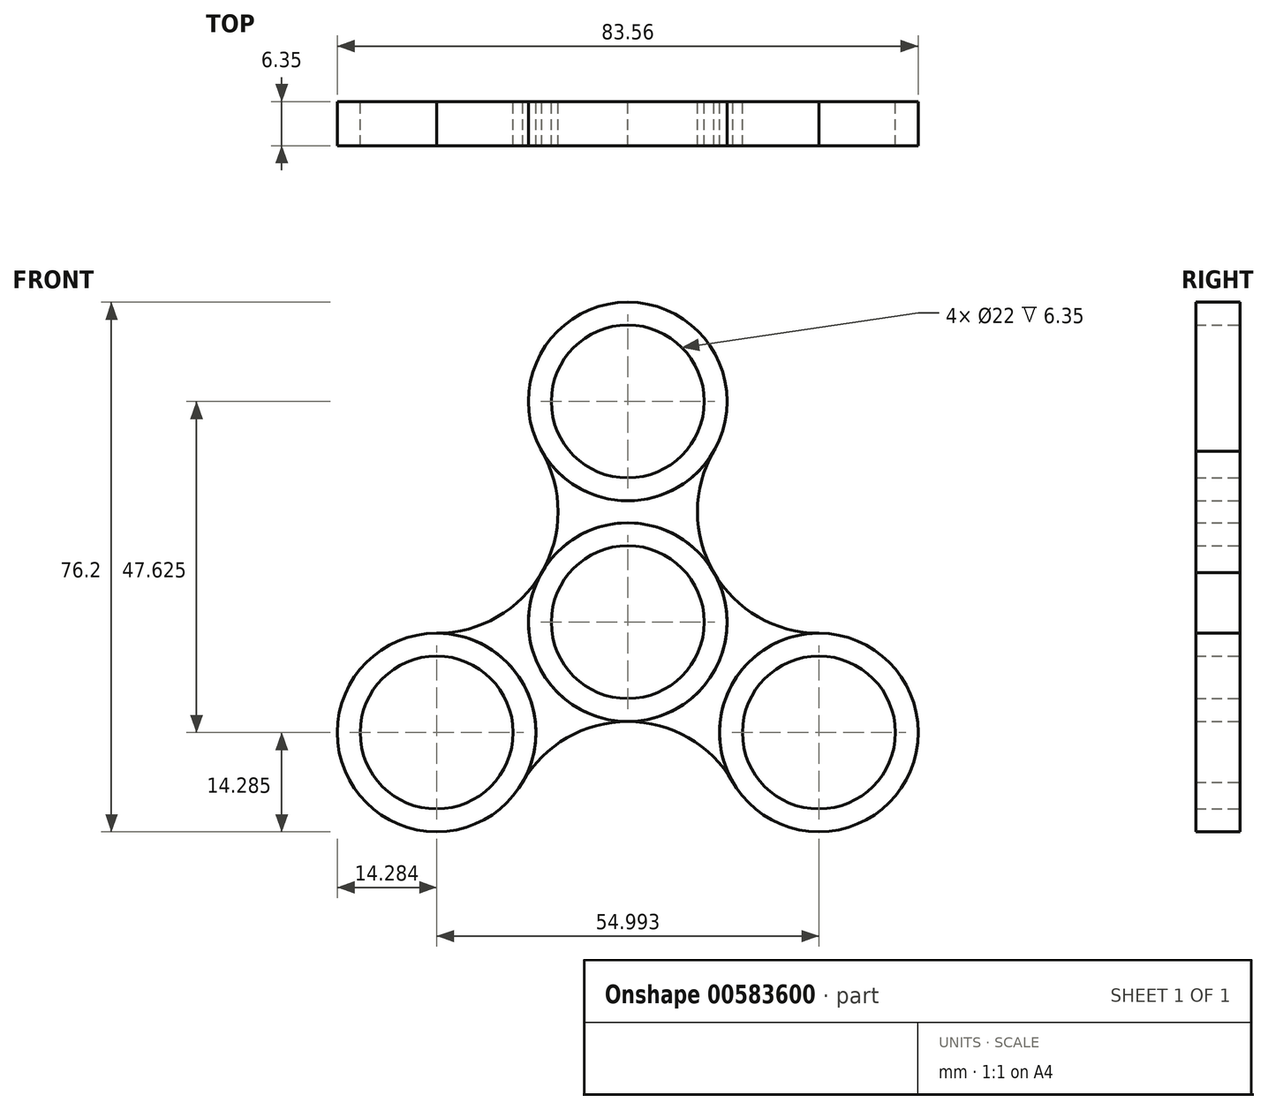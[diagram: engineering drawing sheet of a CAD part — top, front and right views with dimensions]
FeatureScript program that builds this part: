
annotation { "Feature Type Name" : "Feature", "Feature Type Description" : "" }
export const myFeature = defineFeature(function(context is Context, id is Id, definition is map)
    precondition{}
    {
        {
            var Q0;
            Q0=qCreatedBy(makeId("Front.planeOp"),FACE);
            var sketch = newSketch(context, id + "F0", { "sketchPlane" : qUnion([Q0])});
            skCircle(sketch, "E0", {"center": v(0, 0) * mm, "radius": 14.29 * mm});
            skCircle(sketch, "E1", {"center": v(0, 0) * mm, "radius": 11 * mm});
            skCircle(sketch, "E2", {"center": v(0, 31.75) * mm, "radius": 14.29 * mm});
            skCircle(sketch, "E3", {"center": v(0, 31.75) * mm, "radius": 11 * mm});
            skCircle(sketch, "E4.1.0", {"center": v(-27.5, -15.87) * mm, "radius": 11 * mm});
            skCircle(sketch, "E4.1.1", {"center": v(-27.5, -15.87) * mm, "radius": 14.29 * mm});
            skCircle(sketch, "E4.2.0", {"center": v(27.5, -15.88) * mm, "radius": 11 * mm});
            skCircle(sketch, "E4.2.1", {"center": v(27.5, -15.88) * mm, "radius": 14.29 * mm});
            skSolve(sketch);
        }
        {
            var Q0;
            Q0=qCreatedBy(makeId("Front.planeOp"),FACE);
            var sketch = newSketch(context, id + "F1", { "sketchPlane" : qUnion([Q0])});
            skCircle(sketch, "E5.0", {"center": v(0, 31.75) * mm, "radius": 14.29 * mm});
            skCircle(sketch, "E6.0", {"center": v(0, 31.75) * mm, "radius": 11 * mm});
            skCircle(sketch, "E7.0", {"center": v(0, 0) * mm, "radius": 14.29 * mm});
            skCircle(sketch, "E8.0", {"center": v(0, 0) * mm, "radius": 11 * mm});
            skCircle(sketch, "E9.0", {"center": v(27.5, -15.88) * mm, "radius": 14.29 * mm});
            skCircle(sketch, "E10.0", {"center": v(27.5, -15.88) * mm, "radius": 11 * mm});
            skCircle(sketch, "E11.0", {"center": v(-27.5, -15.87) * mm, "radius": 11 * mm});
            skCircle(sketch, "E12.0", {"center": v(-27.5, -15.87) * mm, "radius": 14.29 * mm});
            skArc(sketch, "E13", {"start": v(12.37, 24.6) * mm, "mid": v(12.37, 7.14) * mm, "end": v(27.5, -1.59) * mm});
            skArc(sketch, "E14", {"start": v(-27.5, -1.59) * mm, "mid": v(-12.37, 7.14) * mm, "end": v(-12.37, 24.6) * mm});
            skArc(sketch, "E15", {"start": v(15.12, -23.02) * mm, "mid": v(0, -14.29) * mm, "end": v(-15.12, -23.02) * mm});
            skSolve(sketch);
        }
        {
            var Q0;
            {var subQ0=sQuery(id+"F1.wireOp",EDGE,"E5.0");var subQ1=sQuery(id+"F1.wireOp",EDGE,"E13");var subQ2=makeQuery(id+"F1.imprint","INTERSECT",VERTEX,{"derivedFrom":[subQ1,subQ0]});Q0=makeQuery(id+"F1.imprint","IMPRINT",FACE,{"disambiguationData":[TD([[makeQuery(id+"F1.imprint","IMPRINT",EDGE,{"disambiguationData":[TD([[subQ2,-1.0]])],"derivedFrom":subQ1}),-1.0]])]});}
            var Q1;
            {var subQ0=sQuery(id+"F1.wireOp",EDGE,"E9.0");var subQ1=sQuery(id+"F1.wireOp",EDGE,"E13");var subQ2=makeQuery(id+"F1.imprint","INTERSECT",VERTEX,{"derivedFrom":[subQ1,subQ0]});Q1=makeQuery(id+"F1.imprint","IMPRINT",FACE,{"disambiguationData":[TD([[makeQuery(id+"F1.imprint","IMPRINT",EDGE,{"disambiguationData":[TD([[subQ2,1.0]])],"derivedFrom":subQ1}),-1.0]])]});}
            var Q2;
            {var subQ0=sQuery(id+"F1.wireOp",EDGE,"E12.0");var subQ1=sQuery(id+"F1.wireOp",EDGE,"E14");var subQ2=makeQuery(id+"F1.imprint","INTERSECT",VERTEX,{"derivedFrom":[subQ1,subQ0]});Q2=makeQuery(id+"F1.imprint","IMPRINT",FACE,{"disambiguationData":[TD([[makeQuery(id+"F1.imprint","IMPRINT",EDGE,{"disambiguationData":[TD([[subQ2,-1.0]])],"derivedFrom":subQ1}),-1.0]])]});}
            extrude(context, id + "F2", {"entities" : qUnion([Q0, Q1, Q2]), "depth" : 6.35 * mm, "offsetDistance" : 25.4 * mm});
        }
        {
            var Q0;
            Q0=makeQuery(id+"F0.imprint","IMPRINT",FACE,{"disambiguationData":[TD([[makeQuery(id+"F0.imprint","IMPRINT",EDGE,{"derivedFrom":sQuery(id+"F0.wireOp",EDGE,"E0")}),1.0]])]});
            var Q1;
            Q1=makeQuery(id+"F0.imprint","IMPRINT",FACE,{"disambiguationData":[TD([[makeQuery(id+"F0.imprint","IMPRINT",EDGE,{"derivedFrom":sQuery(id+"F0.wireOp",EDGE,"E2")}),1.0]])]});
            var Q2;
            Q2=makeQuery(id+"F0.imprint","IMPRINT",FACE,{"disambiguationData":[TD([[makeQuery(id+"F0.imprint","IMPRINT",EDGE,{"derivedFrom":sQuery(id+"F0.wireOp",EDGE,"E4.1.0")}),-1.0]])]});
            var Q3;
            Q3=makeQuery(id+"F0.imprint","IMPRINT",FACE,{"disambiguationData":[TD([[makeQuery(id+"F0.imprint","IMPRINT",EDGE,{"derivedFrom":sQuery(id+"F0.wireOp",EDGE,"E4.2.0")}),-1.0]])]});
            extrude(context, id + "F3", {"entities" : qUnion([Q0, Q1, Q2, Q3]), "depth" : 6.35 * mm, "offsetDistance" : 25.4 * mm});
        }
    });
